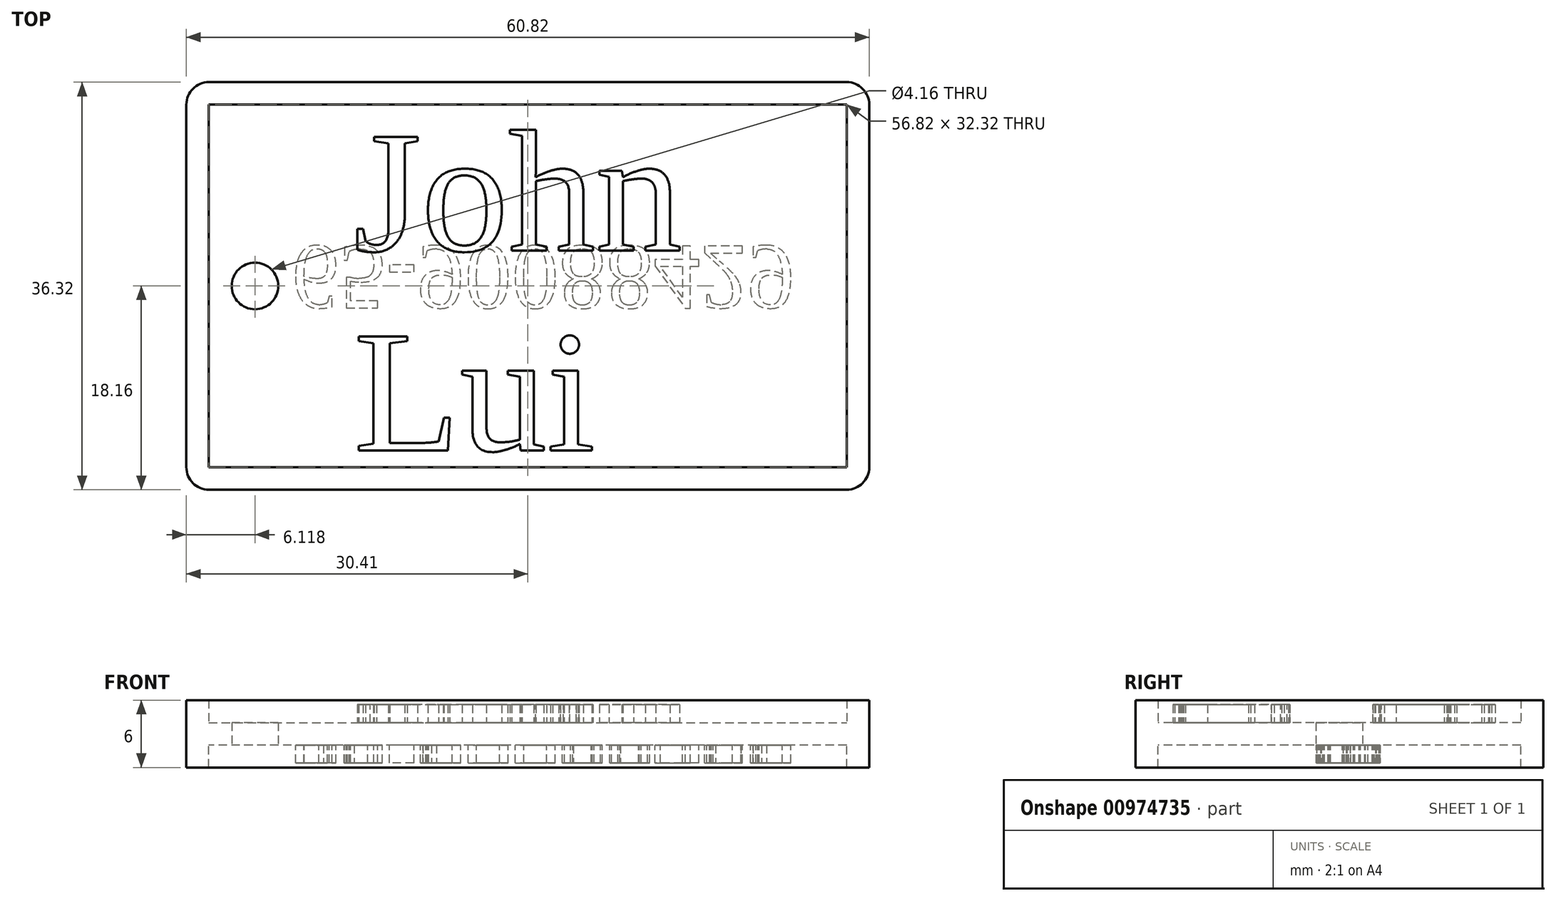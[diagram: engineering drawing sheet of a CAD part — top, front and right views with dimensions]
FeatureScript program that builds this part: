
annotation { "Feature Type Name" : "Feature", "Feature Type Description" : "" }
export const myFeature = defineFeature(function(context is Context, id is Id, definition is map)
    precondition{}
    {
        {
            var Q0;
            Q0=qCreatedBy(makeId("Top.planeOp"),FACE);
            var sketch = newSketch(context, id + "F0", { "sketchPlane" : qUnion([Q0])});
            skLineSegment(sketch, "E0.bottom", {"start": v(-28.41, 18.16) * mm, "end": v(28.41, 18.16) * mm});
            skLineSegment(sketch, "E0.top", {"start": v(-28.41, -18.16) * mm, "end": v(28.41, -18.16) * mm});
            skLineSegment(sketch, "E0.left", {"start": v(-30.41, 16.16) * mm, "end": v(-30.41, -16.16) * mm});
            skLineSegment(sketch, "E0.right", {"start": v(30.41, 16.16) * mm, "end": v(30.41, -16.16) * mm});
            skPoint(sketch, "E0.middle", {"position": v(0, 0) * mm});
            skPoint(sketch, "E1.visualSharp", {"position": v(-30.41, 18.16) * mm});
            skArc(sketch, "E1.filletArc", {"start": v(-28.41, 18.16) * mm, "mid": v(-29.82, 17.57) * mm, "end": v(-30.41, 16.16) * mm});
            skPoint(sketch, "E2.visualSharp", {"position": v(30.41, 18.16) * mm});
            skArc(sketch, "E2.filletArc", {"start": v(30.41, 16.16) * mm, "mid": v(29.82, 17.57) * mm, "end": v(28.41, 18.16) * mm});
            skPoint(sketch, "E3.visualSharp", {"position": v(30.41, -18.16) * mm});
            skArc(sketch, "E3.filletArc", {"start": v(28.41, -18.16) * mm, "mid": v(29.82, -17.57) * mm, "end": v(30.41, -16.16) * mm});
            skLineSegment(sketch, "E4.0", {"start": v(-28.41, 16.16) * mm, "end": v(28.41, 16.16) * mm});
            skLineSegment(sketch, "E4.1", {"start": v(-28.41, 16.16) * mm, "end": v(-28.41, -16.16) * mm});
            skLineSegment(sketch, "E4.2", {"start": v(-28.41, -16.16) * mm, "end": v(28.41, -16.16) * mm});
            skLineSegment(sketch, "E4.3", {"start": v(28.41, 16.16) * mm, "end": v(28.41, -16.16) * mm});
            skPoint(sketch, "E5.visualSharp", {"position": v(-30.41, -18.16) * mm});
            skArc(sketch, "E5.filletArc", {"start": v(-30.41, -16.16) * mm, "mid": v(-29.82, -17.57) * mm, "end": v(-28.41, -18.16) * mm});
            skCircle(sketch, "E6", {"center": v(-24.3, 0) * mm, "radius": 2.08 * mm});
            skSolve(sketch);
        }
        {
            var Q0;
            Q0=makeQuery(id+"F0.imprint","IMPRINT",FACE,{"disambiguationData":[TD([[makeQuery(id+"F0.imprint","IMPRINT",EDGE,{"derivedFrom":sQuery(id+"F0.wireOp",EDGE,"E4.0")}),-1.0]])]});
            extrude(context, id + "F1", {"entities" : qUnion([Q0]), "depth" : 2 * mm, "offsetDistance" : 25 * mm});
        }
        {
            var Q0;
            Q0 = qSketchRegion(id + "F0", true);
            extrude(context, id + "F2", {"entities" : qUnion([Q0]), "operationType" : NewBodyOperationType.ADD, "depth" : 4 * mm, "offsetDistance" : 25 * mm});
        }
        {
            var Q0;
            Q0=makeQuery(id+"F1.opExtrude","CAP_FACE",FACE,{"disambiguationData":[OSD([sQuery(id+"F0.wireOp",EDGE,"E4.0"),sQuery(id+"F0.wireOp",EDGE,"E4.1"),sQuery(id+"F0.wireOp",EDGE,"E4.2"),sQuery(id+"F0.wireOp",EDGE,"E4.3"),sQuery(id+"F0.wireOp",EDGE,"E6")])],"isStart":false});
            var sketch = newSketch(context, id + "F3", { "sketchPlane" : qUnion([Q0])});
            skText(sketch, "E7", { "text": "John\nLui", "fontName": "Tinos-Regular.ttf"});
            const initialGuessF3  = {"E7": [-0.0155, 0.00315, 1, 0, 0.01115]};
            skSetInitialGuess(sketch, initialGuessF3);
            skSolve(sketch);
        }
        {
            var Q0;
            Q0 = qSketchRegion(id + "F3", true);
            extrude(context, id + "F4", {"entities" : qUnion([Q0]), "operationType" : NewBodyOperationType.ADD, "depth" : 1.6 * mm, "offsetDistance" : 25 * mm});
        }
        {
            var Q0;
            {var subQ0=sQuery(id+"F0.wireOp",EDGE,"E4.3");var subQ1=sQuery(id+"F0.wireOp",EDGE,"E4.2");var subQ2=sQuery(id+"F0.wireOp",EDGE,"E4.1");var subQ3=sQuery(id+"F0.wireOp",EDGE,"E4.0");Q0=makeQuery(id+"F2.boolean.opBoolean","MERGE",FACE,{"derivedFrom":[makeQuery(id+"F1.opExtrude","CAP_FACE",FACE,{"disambiguationData":[OSD([subQ3,subQ2,subQ1,subQ0,sQuery(id+"F0.wireOp",EDGE,"E6")])],"isStart":true}),makeQuery(id+"F2.opExtrude","CAP_FACE",FACE,{"disambiguationData":[OSD([sQuery(id+"F0.wireOp",EDGE,"E0.bottom"),sQuery(id+"F0.wireOp",EDGE,"E0.top"),sQuery(id+"F0.wireOp",EDGE,"E0.left"),sQuery(id+"F0.wireOp",EDGE,"E0.right"),sQuery(id+"F0.wireOp",EDGE,"E1.filletArc"),sQuery(id+"F0.wireOp",EDGE,"E2.filletArc"),sQuery(id+"F0.wireOp",EDGE,"E3.filletArc"),subQ3,subQ2,subQ1,subQ0,sQuery(id+"F0.wireOp",EDGE,"E5.filletArc")])],"isStart":true})]});}
            var sketch = newSketch(context, id + "F5", { "sketchPlane" : qUnion([Q0])});
            skLineSegment(sketch, "E8.bottom", {"start": v(28.41, -18.16) * mm, "end": v(-28.41, -18.16) * mm});
            skLineSegment(sketch, "E8.top", {"start": v(28.41, 18.16) * mm, "end": v(-28.41, 18.16) * mm});
            skLineSegment(sketch, "E8.left", {"start": v(30.41, -16.16) * mm, "end": v(30.41, 16.16) * mm});
            skLineSegment(sketch, "E8.right", {"start": v(-30.41, -16.16) * mm, "end": v(-30.41, 16.16) * mm});
            skPoint(sketch, "E8.middle", {"position": v(0, 0) * mm});
            skPoint(sketch, "E9.visualSharp", {"position": v(30.41, -18.16) * mm});
            skArc(sketch, "E9.filletArc", {"start": v(28.41, -18.16) * mm, "mid": v(29.82, -17.57) * mm, "end": v(30.41, -16.16) * mm});
            skPoint(sketch, "E10.visualSharp", {"position": v(-30.41, -18.16) * mm});
            skArc(sketch, "E10.filletArc", {"start": v(-30.41, -16.16) * mm, "mid": v(-29.82, -17.57) * mm, "end": v(-28.41, -18.16) * mm});
            skPoint(sketch, "E11.visualSharp", {"position": v(-30.41, 18.16) * mm});
            skArc(sketch, "E11.filletArc", {"start": v(-28.41, 18.16) * mm, "mid": v(-29.82, 17.57) * mm, "end": v(-30.41, 16.16) * mm});
            skPoint(sketch, "E12.visualSharp", {"position": v(30.41, 18.16) * mm});
            skArc(sketch, "E12.filletArc", {"start": v(30.41, 16.16) * mm, "mid": v(29.82, 17.57) * mm, "end": v(28.41, 18.16) * mm});
            skLineSegment(sketch, "E13.0", {"start": v(28.41, 16.16) * mm, "end": v(-28.41, 16.16) * mm});
            skLineSegment(sketch, "E13.1", {"start": v(28.41, -16.16) * mm, "end": v(28.41, 16.16) * mm});
            skLineSegment(sketch, "E13.2", {"start": v(28.41, -16.16) * mm, "end": v(-28.41, -16.16) * mm});
            skLineSegment(sketch, "E13.3", {"start": v(-28.41, -16.16) * mm, "end": v(-28.41, 16.16) * mm});
            skText(sketch, "E14", { "text": "65-90088429", "fontName": "Tinos-Regular.ttf"});
            const initialGuessF5  = {"E14": [-0.02104, -0.00355, 1, 0, 0.00605]};
            skSetInitialGuess(sketch, initialGuessF5);
            skSolve(sketch);
        }
        {
            var Q0;
            Q0=makeQuery(id+"F5.imprint","IMPRINT",FACE,{"disambiguationData":[TD([[makeQuery(id+"F5.imprint","IMPRINT",EDGE,{"derivedFrom":sQuery(id+"F5.wireOp",EDGE,"E8.bottom")}),1.0]])]});
            extrude(context, id + "F6", {"entities" : qUnion([Q0]), "operationType" : NewBodyOperationType.ADD, "depth" : 2 * mm, "offsetDistance" : 25 * mm});
        }
        {
            var Q0;
            Q0=makeQuery(id+"F5.imprint","IMPRINT",FACE,{"disambiguationData":[TD([[makeQuery(id+"F5.imprint","IMPRINT",EDGE,{"derivedFrom":sQuery(id+"F5.wireOp",EDGE,"E14.sketch_text.stroke-25")}),-1.0]])]});
            var Q1;
            Q1=makeQuery(id+"F5.imprint","IMPRINT",FACE,{"disambiguationData":[TD([[makeQuery(id+"F5.imprint","IMPRINT",EDGE,{"derivedFrom":sQuery(id+"F5.wireOp",EDGE,"E14.sketch_text.stroke-0")}),-1.0]])]});
            var Q2;
            Q2=makeQuery(id+"F5.imprint","IMPRINT",FACE,{"disambiguationData":[TD([[makeQuery(id+"F5.imprint","IMPRINT",EDGE,{"derivedFrom":sQuery(id+"F5.wireOp",EDGE,"E14.sketch_text.stroke-48")}),-1.0]])]});
            var Q3;
            Q3=makeQuery(id+"F5.imprint","IMPRINT",FACE,{"disambiguationData":[TD([[makeQuery(id+"F5.imprint","IMPRINT",EDGE,{"derivedFrom":sQuery(id+"F5.wireOp",EDGE,"E14.sketch_text.stroke-52")}),-1.0]])]});
            var Q4;
            Q4=makeQuery(id+"F5.imprint","IMPRINT",FACE,{"disambiguationData":[TD([[makeQuery(id+"F5.imprint","IMPRINT",EDGE,{"derivedFrom":sQuery(id+"F5.wireOp",EDGE,"E14.sketch_text.stroke-75")}),-1.0]])]});
            var Q5;
            Q5=makeQuery(id+"F5.imprint","IMPRINT",FACE,{"disambiguationData":[TD([[makeQuery(id+"F5.imprint","IMPRINT",EDGE,{"derivedFrom":sQuery(id+"F5.wireOp",EDGE,"E14.sketch_text.stroke-90")}),-1.0]])]});
            var Q6;
            Q6=makeQuery(id+"F5.imprint","IMPRINT",FACE,{"disambiguationData":[TD([[makeQuery(id+"F5.imprint","IMPRINT",EDGE,{"derivedFrom":sQuery(id+"F5.wireOp",EDGE,"E14.sketch_text.stroke-105")}),-1.0]])]});
            var Q7;
            Q7=makeQuery(id+"F5.imprint","IMPRINT",FACE,{"disambiguationData":[TD([[makeQuery(id+"F5.imprint","IMPRINT",EDGE,{"derivedFrom":sQuery(id+"F5.wireOp",EDGE,"E14.sketch_text.stroke-136")}),-1.0]])]});
            var Q8;
            Q8=makeQuery(id+"F5.imprint","IMPRINT",FACE,{"disambiguationData":[TD([[makeQuery(id+"F5.imprint","IMPRINT",EDGE,{"derivedFrom":sQuery(id+"F5.wireOp",EDGE,"E14.sketch_text.stroke-167")}),-1.0]])]});
            var Q9;
            Q9=makeQuery(id+"F5.imprint","IMPRINT",FACE,{"disambiguationData":[TD([[makeQuery(id+"F5.imprint","IMPRINT",EDGE,{"derivedFrom":sQuery(id+"F5.wireOp",EDGE,"E14.sketch_text.stroke-182")}),-1.0]])]});
            var Q10;
            Q10=makeQuery(id+"F5.imprint","IMPRINT",FACE,{"disambiguationData":[TD([[makeQuery(id+"F5.imprint","IMPRINT",EDGE,{"derivedFrom":sQuery(id+"F5.wireOp",EDGE,"E14.sketch_text.stroke-204")}),-1.0]])]});
            extrude(context, id + "F7", {"entities" : qUnion([Q0, Q1, Q2, Q3, Q4, Q5, Q6, Q7, Q8, Q9, Q10]), "operationType" : NewBodyOperationType.ADD, "depth" : 1.6 * mm, "offsetDistance" : 25 * mm});
        }
    });
